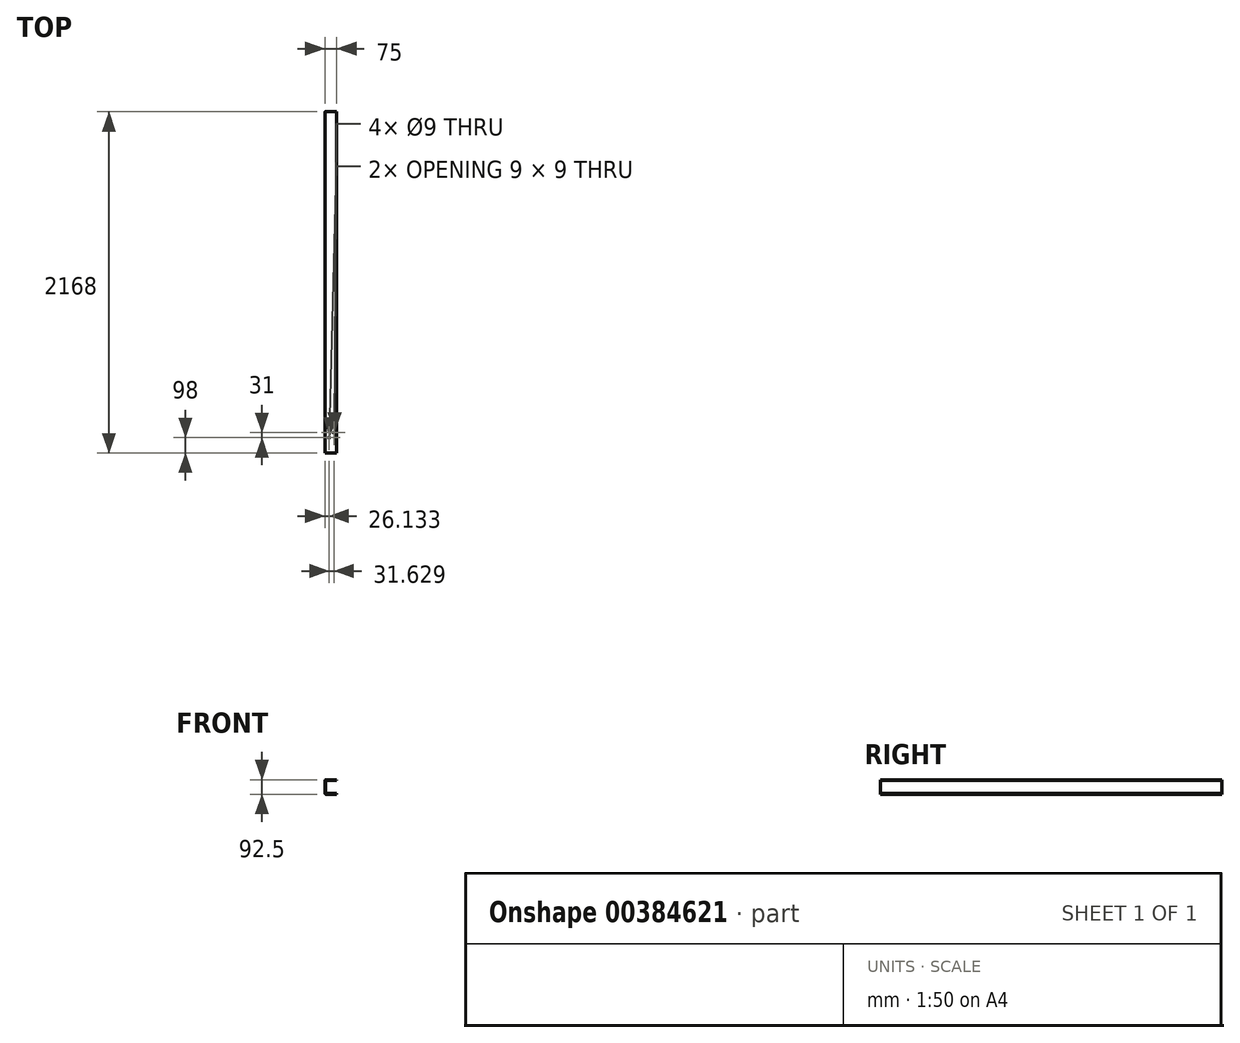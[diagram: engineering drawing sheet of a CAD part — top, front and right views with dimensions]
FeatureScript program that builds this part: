
annotation { "Feature Type Name" : "Feature", "Feature Type Description" : "" }
export const myFeature = defineFeature(function(context is Context, id is Id, definition is map)
    precondition{}
    {
        {
            var Q0;
            Q0=qCreatedBy(makeId("Front.planeOp"),FACE);
            var sketch = newSketch(context, id + "F0", { "sketchPlane" : qUnion([Q0])});
            skLineSegment(sketch, "E0.bottom", {"start": v(-37.5, -46.25) * mm, "end": v(29.5, -46.25) * mm});
            skLineSegment(sketch, "E0.top", {"start": v(-37.5, 46.25) * mm, "end": v(29.5, 46.25) * mm});
            skLineSegment(sketch, "E0.left", {"start": v(-37.5, -46.25) * mm, "end": v(-37.5, -42.25) * mm});
            skLineSegment(sketch, "E0.right", {"start": v(37.5, -38.25) * mm, "end": v(37.5, 38.25) * mm});
            skPoint(sketch, "E0.middle", {"position": v(0, 0) * mm});
            skLineSegment(sketch, "E1", {"start": v(-37.5, 42.25) * mm, "end": v(29.5, 42.25) * mm});
            skLineSegment(sketch, "E2", {"start": v(33.5, 38.25) * mm, "end": v(33.5, -38.25) * mm});
            skLineSegment(sketch, "E3", {"start": v(29.5, -42.25) * mm, "end": v(-37.5, -42.25) * mm});
            skLineSegment(sketch, "E4.trimOffspring", {"start": v(-37.5, 42.25) * mm, "end": v(-37.5, 46.25) * mm});
            skPoint(sketch, "E5.visualSharp", {"position": v(33.5, 42.25) * mm});
            skArc(sketch, "E5.filletArc", {"start": v(33.5, 38.25) * mm, "mid": v(32.33, 41.08) * mm, "end": v(29.5, 42.25) * mm});
            skPoint(sketch, "E6.visualSharp", {"position": v(33.5, -42.25) * mm});
            skArc(sketch, "E6.filletArc", {"start": v(29.5, -42.25) * mm, "mid": v(32.33, -41.08) * mm, "end": v(33.5, -38.25) * mm});
            skPoint(sketch, "E7.visualSharp", {"position": v(37.5, 46.25) * mm});
            skArc(sketch, "E7.filletArc", {"start": v(37.5, 38.25) * mm, "mid": v(35.16, 43.9) * mm, "end": v(29.5, 46.25) * mm});
            skPoint(sketch, "E8.visualSharp", {"position": v(37.5, -46.25) * mm});
            skArc(sketch, "E8.filletArc", {"start": v(29.5, -46.25) * mm, "mid": v(35.16, -43.9) * mm, "end": v(37.5, -38.25) * mm});
            skSolve(sketch);
        }
        {
            var Q0;
            Q0=qSketchRegion(id+"F0",true);
            extrude(context, id + "F1", {"entities" : qUnion([Q0]), "oppositeDirection" : true, "depth" : 2168 * mm});
        }
        {
            var Q0;
            Q0=qCreatedBy(makeId("Top.planeOp"),FACE);
            var sketch = newSketch(context, id + "F2", { "sketchPlane" : qUnion([Q0])});
            skPoint(sketch, "E9.start.orphan", {"position": v(62.21, -83.5) * mm});
            skPoint(sketch, "E10.start.orphan", {"position": v(62.21, 0) * mm});
            skPoint(sketch, "E11.start.orphan", {"position": v(-63.34, 0) * mm});
            skPoint(sketch, "E12.trimOffspring.end.orphan", {"position": v(0, 45.5) * mm});
            skPoint(sketch, "E13.orphan", {"position": v(0, 14.5) * mm});
            skSolve(sketch);
        }
        {
            var Q0;
            Q0=qCreatedBy(makeId("Top.planeOp"),FACE);
            var Q1;
            Q1=qBodyType(qCreatedBy(id+"FbHpdg401B42YHa",EDGE),BodyType.WIRE);
            cPlane(context, id + "F3", {"entities" : qUnion([Q0, Q1]), "cplaneType" : CPlaneType.OFFSET, "offset" : 46.25 * mm, "width" : 150 * mm, "height" : 150 * mm});
        }
        {
            var Q0;
            Q0=qCreatedBy(id+"F3.planeOp",FACE);
            var sketch = newSketch(context, id + "F4", { "sketchPlane" : qUnion([Q0])});
            skLineSegment(sketch, "E14", {"start": v(0, 0) * mm, "end": v(0, 83.5) * mm});
            skLineSegment(sketch, "E15", {"start": v(0, 83.5) * mm, "end": v(-41.75, 83.5) * mm});
            skLineSegment(sketch, "E16", {"start": v(-41.75, 0) * mm, "end": v(0, 0) * mm});
            skLineSegment(sketch, "E17", {"start": v(0, 83.5) * mm, "end": v(41.75, 83.5) * mm});
            skLineSegment(sketch, "E18", {"start": v(41.75, 0) * mm, "end": v(0, 0) * mm});
            skLineSegment(sketch, "E19", {"start": v(-26.25, 0) * mm, "end": v(-26.25, 14.25) * mm});
            skLineSegment(sketch, "E20", {"start": v(-26.25, 14.25) * mm, "end": v(21.75, 14.25) * mm});
            skLineSegment(sketch, "E21", {"start": v(26.25, 69.25) * mm, "end": v(0, 69.25) * mm});
            skLineSegment(sketch, "E22.trimOffspring", {"start": v(26.25, 69.25) * mm, "end": v(26.25, 83.5) * mm});
            skLineSegment(sketch, "E23", {"start": v(0, 83.5) * mm, "end": v(0, 158) * mm});
            skLineSegment(sketch, "E24", {"start": v(0, 158) * mm, "end": v(-30, 158) * mm});
            skLineSegment(sketch, "E25", {"start": v(0, 158) * mm, "end": v(30, 158) * mm});
            skLineSegment(sketch, "E26", {"start": v(30, 158) * mm, "end": v(30, 100.42) * mm});
            skLineSegment(sketch, "E27", {"start": v(-30, 158) * mm, "end": v(-30, 98) * mm});
            skLineSegment(sketch, "E28", {"start": v(-15.5, 115.34) * mm, "end": v(0, 115.34) * mm});
            skLineSegment(sketch, "E29", {"start": v(30, 158) * mm, "end": v(30, 143.5) * mm});
            skPoint(sketch, "E30.endSnap0", {"position": v(15, 158) * mm});
            skLineSegment(sketch, "E31", {"start": v(0, 115.34) * mm, "end": v(-15.5, 115.34) * mm});
            skLineSegment(sketch, "E32", {"start": v(-15.5, 115.34) * mm, "end": v(-15.5, 102.5) * mm});
            skPoint(sketch, "E33.orphan", {"position": v(30, 115.34) * mm});
            skPoint(sketch, "E30.end.orphan", {"position": v(15.5, 158) * mm});
            skPoint(sketch, "E34.start.orphan", {"position": v(0, 146.34) * mm});
            skPoint(sketch, "E35.end.orphan", {"position": v(-30, 115.34) * mm});
            skLineSegment(sketch, "E36", {"start": v(0, 158) * mm, "end": v(15.5, 158) * mm});
            skLineSegment(sketch, "E37", {"start": v(15.5, 158) * mm, "end": v(15.5, 133.5) * mm});
            skLineSegment(sketch, "E38", {"start": v(15.5, 83.5) * mm, "end": v(15.5, 93.5) * mm});
            skLineSegment(sketch, "E39.trimOffspring", {"start": v(15.5, 124.5) * mm, "end": v(15.5, 112.2) * mm});
            skLineSegment(sketch, "E40", {"start": v(-15.5, 98) * mm, "end": v(0, 98) * mm});
            skLineSegment(sketch, "E41.trimOffspring", {"start": v(15.5, 102.5) * mm, "end": v(15.5, 124.5) * mm});
            skLineSegment(sketch, "E42", {"start": v(0, 129) * mm, "end": v(-2, 129) * mm});
            skPoint(sketch, "E43.center.orphan", {"position": v(-15.5, 129) * mm});
            skLineSegment(sketch, "E44", {"start": v(0, 98) * mm, "end": v(6.87, 98) * mm});
            skCircle(sketch, "E45", {"center": v(11.37, 98) * mm, "radius": 4.5 * mm});
            skLineSegment(sketch, "E46", {"start": v(-2, 129) * mm, "end": v(-10.26, 129) * mm});
            skLineSegment(sketch, "E47", {"start": v(-10.26, 129) * mm, "end": v(-10.26, 115.34) * mm});
            skLineSegment(sketch, "E48", {"start": v(-10.26, 129) * mm, "end": v(-11.51, 129) * mm});
            skLineSegment(sketch, "E49.trimOffspring", {"start": v(-16.01, 133.5) * mm, "end": v(-16.01, 142.66) * mm});
            skCircle(sketch, "E50", {"center": v(-20.26, 129) * mm, "radius": 4.5 * mm});
            skPoint(sketch, "E51.start.orphan", {"position": v(-16.01, 129) * mm});
            skSolve(sketch);
        }
        {
            var Q0;
            Q0=makeQuery(id+"F4.imprint","IMPRINT",FACE,{"disambiguationData":[TD([[makeQuery(id+"F4.imprint","IMPRINT",EDGE,{"derivedFrom":sQuery(id+"F4.wireOp",EDGE,"E45")}),1.0]])]});
            var Q1;
            Q1=makeQuery(id+"F4.imprint","IMPRINT",FACE,{"disambiguationData":[TD([[makeQuery(id+"F4.imprint","IMPRINT",EDGE,{"derivedFrom":sQuery(id+"F4.wireOp",EDGE,"E50")}),1.0]])]});
            extrude(context, id + "F5", {"entities" : qUnion([Q0, Q1]), "operationType" : NewBodyOperationType.REMOVE, "endBound" : BoundingType.UP_TO_NEXT, "oppositeDirection" : true, "depth" : 25 * mm});
        }
        {
            var Q0;
            Q0=qCreatedBy(makeId("Right.planeOp"),FACE);
            cPlane(context, id + "F6", {"entities" : qUnion([Q0]), "cplaneType" : CPlaneType.OFFSET, "offset" : 250 * mm, "oppositeDirection" : true, "width" : 150 * mm, "height" : 150 * mm});
        }
        {
            var Q0;
            Q0=makeQuery(id+"F1.opExtrude","SWEPT_BODY",BODY,{"disambiguationData":[OSD([sQuery(id+"F0.wireOp",EDGE,"E0.bottom"),sQuery(id+"F0.wireOp",EDGE,"E0.top"),sQuery(id+"F0.wireOp",EDGE,"E0.left"),sQuery(id+"F0.wireOp",EDGE,"E0.right"),sQuery(id+"F0.wireOp",EDGE,"E1"),sQuery(id+"F0.wireOp",EDGE,"E2"),sQuery(id+"F0.wireOp",EDGE,"E3"),sQuery(id+"F0.wireOp",EDGE,"E4.trimOffspring"),sQuery(id+"F0.wireOp",EDGE,"E5.filletArc"),sQuery(id+"F0.wireOp",EDGE,"E6.filletArc"),sQuery(id+"F0.wireOp",EDGE,"E7.filletArc"),sQuery(id+"F0.wireOp",EDGE,"E8.filletArc")])]});
            var Q1;
            Q1=qCreatedBy(id+"F6.planeOp",FACE);
            mirror(context, id + "F7", {"entities" : qUnion([Q0]), "mirrorPlane" : qUnion([Q1])});
        }
        {
            var Q0;
            Q0=makeQuery(id+"F1.opExtrude","SWEPT_BODY",BODY,{"disambiguationData":[OSD([sQuery(id+"F0.wireOp",EDGE,"E0.bottom"),sQuery(id+"F0.wireOp",EDGE,"E0.top"),sQuery(id+"F0.wireOp",EDGE,"E0.left"),sQuery(id+"F0.wireOp",EDGE,"E0.right"),sQuery(id+"F0.wireOp",EDGE,"E1"),sQuery(id+"F0.wireOp",EDGE,"E2"),sQuery(id+"F0.wireOp",EDGE,"E3"),sQuery(id+"F0.wireOp",EDGE,"E4.trimOffspring"),sQuery(id+"F0.wireOp",EDGE,"E5.filletArc"),sQuery(id+"F0.wireOp",EDGE,"E6.filletArc"),sQuery(id+"F0.wireOp",EDGE,"E7.filletArc"),sQuery(id+"F0.wireOp",EDGE,"E8.filletArc")])]});
            deleteBodies(context, id + "F8", {"entities" : qUnion([Q0])});
        }
    });
